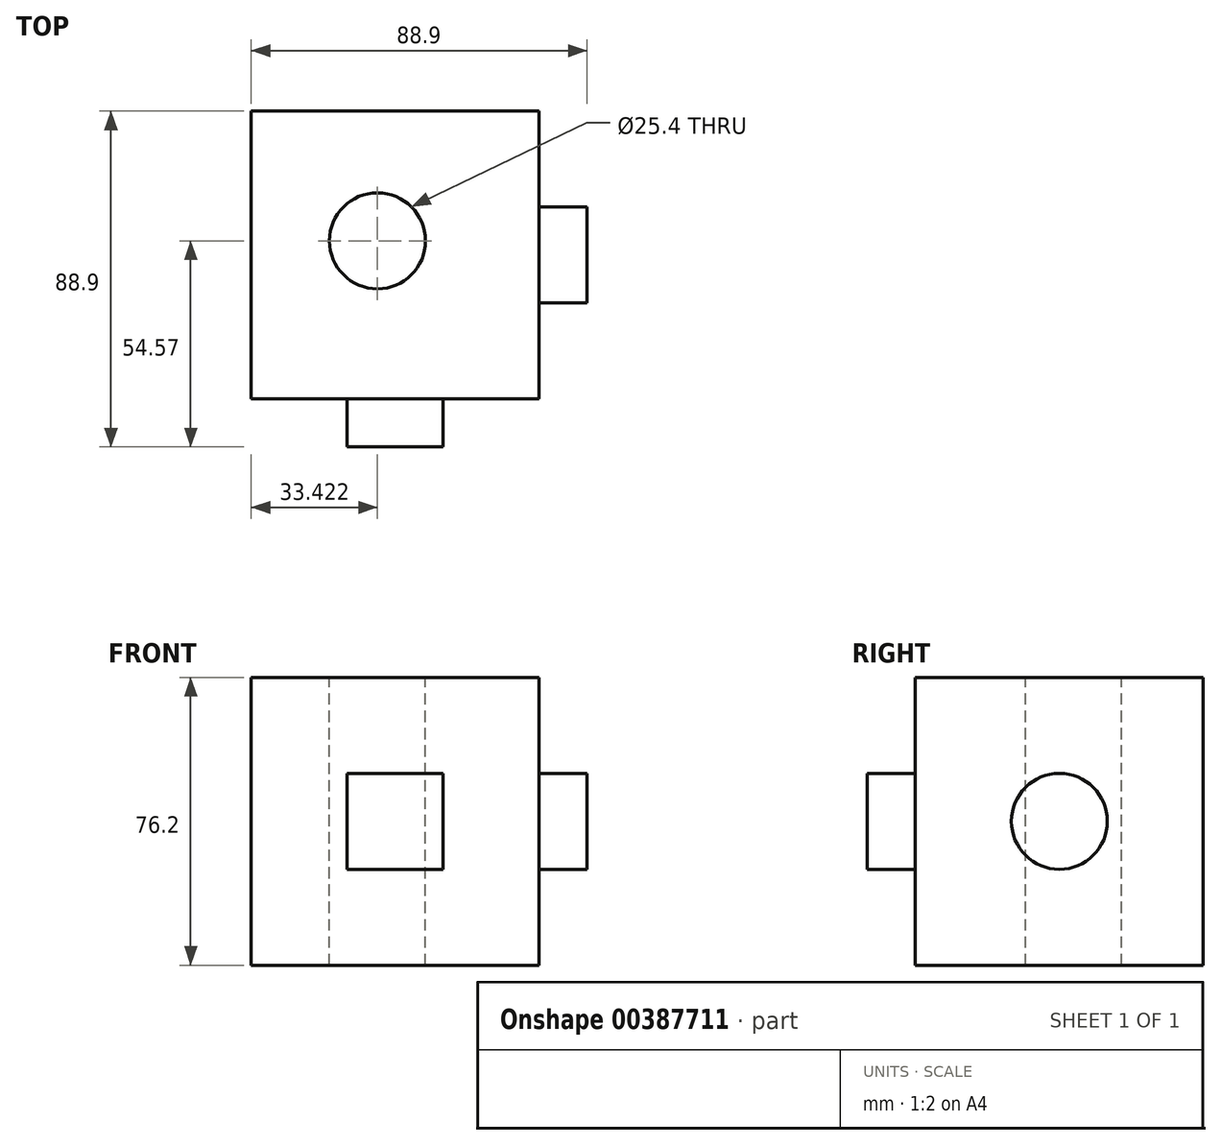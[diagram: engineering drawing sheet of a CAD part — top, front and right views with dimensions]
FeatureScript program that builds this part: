
annotation { "Feature Type Name" : "Feature", "Feature Type Description" : "" }
export const myFeature = defineFeature(function(context is Context, id is Id, definition is map)
    precondition{}
    {
        {
            var Q0;
            Q0=qCreatedBy(makeId("Front.planeOp"),FACE);
            var sketch = newSketch(context, id + "F0", { "sketchPlane" : qUnion([Q0])});
            skLineSegment(sketch, "E0.bottom", {"start": v(0, 0) * mm, "end": v(76.2, 0) * mm});
            skLineSegment(sketch, "E0.top", {"start": v(0, 76.2) * mm, "end": v(76.2, 76.2) * mm});
            skLineSegment(sketch, "E0.left", {"start": v(0, 0) * mm, "end": v(0, 76.2) * mm});
            skLineSegment(sketch, "E0.right", {"start": v(76.2, 0) * mm, "end": v(76.2, 76.2) * mm});
            skSolve(sketch);
        }
        {
            var Q0;
            Q0=makeQuery(id+"F0.imprint","IMPRINT",FACE,{"disambiguationData":[TD([[makeQuery(id+"F0.imprint","IMPRINT",EDGE,{"derivedFrom":sQuery(id+"F0.wireOp",EDGE,"E0.bottom")}),1.0]])]});
            extrude(context, id + "F1", {"entities" : qUnion([Q0]), "depth" : 76.2 * mm});
        }
        {
            var Q0;
            Q0=makeQuery(id+"F1.opExtrude","SWEPT_FACE",FACE,{"disambiguationData":[OSD([sQuery(id+"F0.wireOp",EDGE,"E0.top")])]});
            var sketch = newSketch(context, id + "F2", { "sketchPlane" : qUnion([Q0])});
            skPoint(sketch, "E1", {"position": v(33.42, -34.33) * mm});
            skSolve(sketch);
        }
        {
            var Q0;
            Q0=sQuery(id+"F2.wireOp",VERTEX,"E1");
            var Q1;
            Q1=makeQuery(id+"F1.opExtrude","SWEPT_BODY",BODY,{"disambiguationData":[OSD([sQuery(id+"F0.wireOp",EDGE,"E0.bottom"),sQuery(id+"F0.wireOp",EDGE,"E0.top"),sQuery(id+"F0.wireOp",EDGE,"E0.left"),sQuery(id+"F0.wireOp",EDGE,"E0.right")])]});
            hole(context, id + "F3", {"style" : HoleStyle.SIMPLE, "endStyle" : HoleEndStyle.THROUGH, "holeDiameter" : 25.4 * mm, "isTappedThrough" : true, "tappedDepth" : 12.7 * mm, "tapClearance" : 3, "locations" : qUnion([Q0]), "scope" : qUnion([Q1])});
        }
        {
            var Q0;
            Q0=makeQuery(id+"F1.opExtrude","SWEPT_FACE",FACE,{"disambiguationData":[OSD([sQuery(id+"F0.wireOp",EDGE,"E0.right")])]});
            var sketch = newSketch(context, id + "F4", { "sketchPlane" : qUnion([Q0])});
            skCircle(sketch, "E2", {"center": v(-38.1, 38.1) * mm, "radius": 12.7 * mm});
            skSolve(sketch);
        }
        {
            var Q0;
            Q0=makeQuery(id+"F1.opExtrude","CAP_FACE",FACE,{"disambiguationData":[OSD([sQuery(id+"F0.wireOp",EDGE,"E0.bottom"),sQuery(id+"F0.wireOp",EDGE,"E0.top"),sQuery(id+"F0.wireOp",EDGE,"E0.left"),sQuery(id+"F0.wireOp",EDGE,"E0.right")])],"isStart":false});
            var sketch = newSketch(context, id + "F5", { "sketchPlane" : qUnion([Q0])});
            skLineSegment(sketch, "E3.bottom", {"start": v(50.8, 50.8) * mm, "end": v(25.4, 50.8) * mm});
            skLineSegment(sketch, "E3.top", {"start": v(50.8, 25.4) * mm, "end": v(25.4, 25.4) * mm});
            skLineSegment(sketch, "E3.left", {"start": v(50.8, 50.8) * mm, "end": v(50.8, 25.4) * mm});
            skLineSegment(sketch, "E3.right", {"start": v(25.4, 50.8) * mm, "end": v(25.4, 25.4) * mm});
            skSolve(sketch);
        }
        {
            var Q0;
            Q0=makeQuery(id+"F5.imprint","IMPRINT",FACE,{"disambiguationData":[TD([[makeQuery(id+"F5.imprint","IMPRINT",EDGE,{"derivedFrom":sQuery(id+"F5.wireOp",EDGE,"E3.bottom")}),1.0]])]});
            extrude(context, id + "F6", {"entities" : qUnion([Q0]), "operationType" : NewBodyOperationType.ADD, "depth" : 12.7 * mm});
        }
        {
            var Q0;
            Q0=makeQuery(id+"F4.imprint","IMPRINT",FACE,{"disambiguationData":[TD([[makeQuery(id+"F4.imprint","IMPRINT",EDGE,{"derivedFrom":sQuery(id+"F4.wireOp",EDGE,"E2")}),1.0]])]});
            extrude(context, id + "F7", {"entities" : qUnion([Q0]), "operationType" : NewBodyOperationType.ADD, "depth" : 12.7 * mm});
        }
    });
